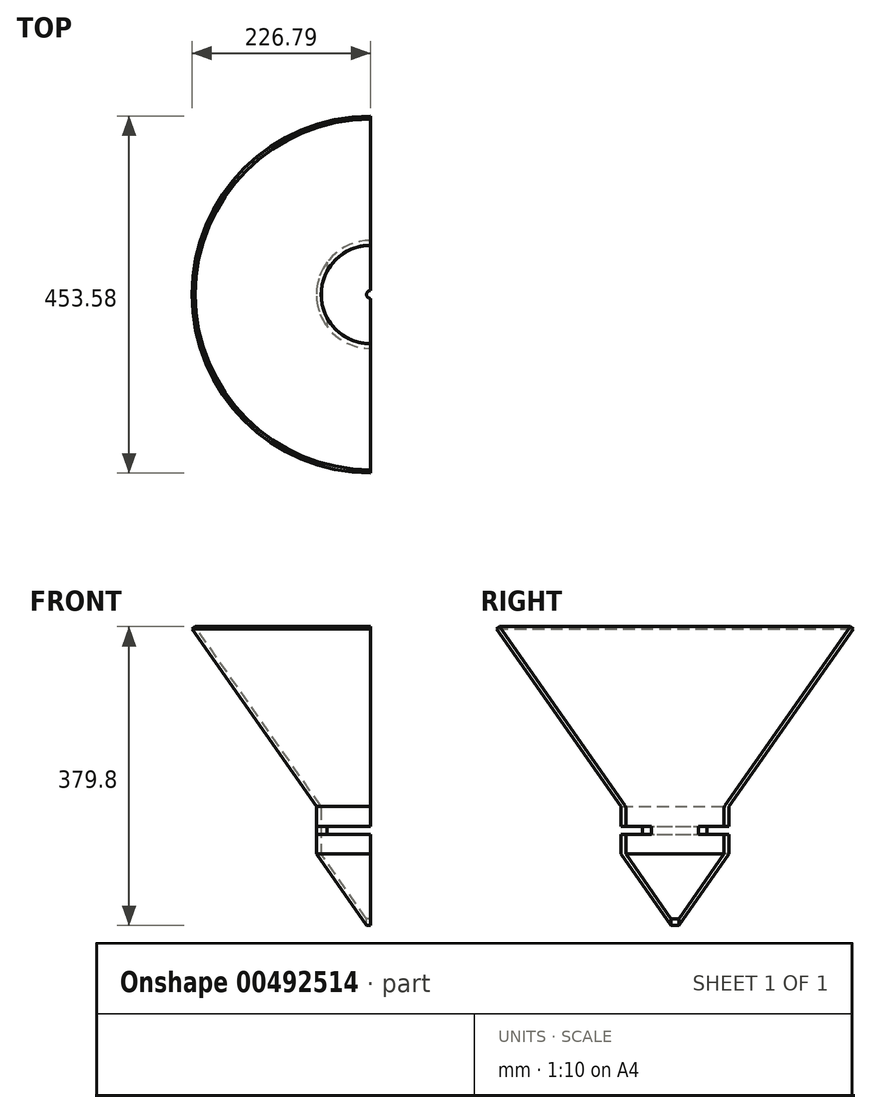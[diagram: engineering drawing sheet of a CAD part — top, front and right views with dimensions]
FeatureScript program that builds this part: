
annotation { "Feature Type Name" : "Feature", "Feature Type Description" : "" }
export const myFeature = defineFeature(function(context is Context, id is Id, definition is map)
    precondition{}
    {
        {
            var Q0;
            Q0=qCreatedBy(makeId("Right.planeOp"),FACE);
            var sketch = newSketch(context, id + "F0", { "sketchPlane" : qUnion([Q0])});
            skLineSegment(sketch, "E0", {"start": v(0, 0) * mm, "end": v(0, 158.91) * mm, "construction": true});
            skLineSegment(sketch, "E1", {"start": v(68.6, 0) * mm, "end": v(226.8, 225.91) * mm});
            skLineSegment(sketch, "E2", {"start": v(63.4, 1.3) * mm, "end": v(222.7, 228.78) * mm});
            skLineSegment(sketch, "E3", {"start": v(62.5, -1.58) * mm, "end": v(62.5, -25.19) * mm});
            skLineSegment(sketch, "E4", {"start": v(68.6, 0) * mm, "end": v(68.6, -25.19) * mm});
            skPoint(sketch, "E5.visualSharp", {"position": v(62.5, 0) * mm});
            skArc(sketch, "E5.filletArc", {"start": v(63.4, 1.3) * mm, "mid": v(62.73, -0.07) * mm, "end": v(62.5, -1.58) * mm});
            skLineSegment(sketch, "E6", {"start": v(62.5, -25.19) * mm, "end": v(68.6, -25.19) * mm});
            skLineSegment(sketch, "E7", {"start": v(222.7, 228.78) * mm, "end": v(222.7, 228.78) * mm});
            skLineSegment(sketch, "E8", {"start": v(222.7, 228.78) * mm, "end": v(226.8, 225.91) * mm});
            skSolve(sketch);
        }
        {
            var Q0;
            Q0 = qSketchRegion(id + "F0", true);
            var Q1;
            Q1=sQuery(id+"F0.wireOp",EDGE,"E0");
            revolve(context, id + "F1", {"entities" : qUnion([Q0]), "axis" : qUnion([Q1]), "revolveType" : RevolveType.ONE_DIRECTION, "angle" : 180 * degree});
        }
        {
            var Q0;
            Q0=makeQuery(id+"F1.opRevolve","SWEPT_FACE",FACE,{"disambiguationData":[OSD([sQuery(id+"F0.wireOp",EDGE,"E6")])]});
            var sketch = newSketch(context, id + "F2", { "sketchPlane" : qUnion([Q0])});
            skArc(sketch, "E9", {"start": v(0, 68.6) * mm, "mid": v(-68.56, 0) * mm, "end": v(0, -68.6) * mm});
            skArc(sketch, "E10", {"start": v(0, 62.5) * mm, "mid": v(-62.5, 0) * mm, "end": v(0, -62.5) * mm});
            skLineSegment(sketch, "E11", {"start": v(-55, -40.95) * mm, "end": v(-55, 41) * mm});
            skSolve(sketch);
        }
        {
            var Q0;
            {var subQ0=sQuery(id+"F2.wireOp",EDGE,"E11");var subQ1=sQuery(id+"F2.wireOp",EDGE,"E9");var subQ2=makeQuery(id+"F2.imprint","INTERSECT",VERTEX,{"disambiguationData":[OD(0.0)],"derivedFrom":[subQ1,subQ0]});Q0=makeQuery(id+"F2.imprint","IMPRINT",FACE,{"disambiguationData":[TD([[makeQuery(id+"F2.imprint","IMPRINT",EDGE,{"disambiguationData":[TD([[subQ2,1.0]])],"derivedFrom":subQ1}),1.0]])]});}
            extrude(context, id + "F3", {"entities" : qUnion([Q0]), "operationType" : NewBodyOperationType.ADD, "depth" : 10 * mm});
        }
        {
            var Q0;
            Q0=makeQuery(id+"F3.opExtrude","CAP_FACE",FACE,{"disambiguationData":[OSD([sQuery(id+"F2.wireOp",EDGE,"E9"),sQuery(id+"F2.wireOp",EDGE,"E10"),sQuery(id+"F2.wireOp",EDGE,"E11")])],"isStart":false});
            var sketch = newSketch(context, id + "F4", { "sketchPlane" : qUnion([Q0])});
            skArc(sketch, "E12.0", {"start": v(-55, -40.95) * mm, "mid": v(-68.56, 0) * mm, "end": v(-55, 40.95) * mm});
            skLineSegment(sketch, "E12.1", {"start": v(-55, -29.69) * mm, "end": v(-55, -40.95) * mm});
            skLineSegment(sketch, "E12.2", {"start": v(-55, 40.95) * mm, "end": v(-55, 29.69) * mm});
            skArc(sketch, "E12.3", {"start": v(0, -62.5) * mm, "mid": v(-32.02, -53.67) * mm, "end": v(-55, -29.69) * mm});
            skArc(sketch, "E12.4", {"start": v(-55, 29.69) * mm, "mid": v(-32.02, 53.67) * mm, "end": v(0, 62.5) * mm});
            skLineSegment(sketch, "E12.5", {"start": v(0, 62.5) * mm, "end": v(0, 68.6) * mm});
            skArc(sketch, "E12.6", {"start": v(0, 68.6) * mm, "mid": v(-68.6, 0) * mm, "end": v(0, -68.6) * mm});
            skLineSegment(sketch, "E12.7", {"start": v(0, -68.6) * mm, "end": v(0, -62.5) * mm});
            skArc(sketch, "E13.0", {"start": v(-55, 40.95) * mm, "mid": v(-68.56, 0) * mm, "end": v(-55, -40.95) * mm});
            skLineSegment(sketch, "E13.1", {"start": v(-55, 29.69) * mm, "end": v(-55, 40.95) * mm});
            skArc(sketch, "E13.2", {"start": v(-55, -29.69) * mm, "mid": v(-62.5, 0) * mm, "end": v(-55, 29.69) * mm});
            skLineSegment(sketch, "E13.3", {"start": v(-55, -40.95) * mm, "end": v(-55, -29.69) * mm});
            skSolve(sketch);
        }
        {
            var Q0;
            Q0 = qSketchRegion(id + "F4", true);
            extrude(context, id + "F5", {"entities" : qUnion([Q0]), "operationType" : NewBodyOperationType.ADD, "depth" : 25 * mm});
        }
        {
            var Q0;
            Q0=qCreatedBy(makeId("Front.planeOp"),FACE);
            var sketch = newSketch(context, id + "F6", { "sketchPlane" : qUnion([Q0])});
            skLineSegment(sketch, "E14", {"start": v(0, 0) * mm, "end": v(0, -90.56) * mm, "construction": true});
            skLineSegment(sketch, "E15.0", {"start": v(0, -60.19) * mm, "end": v(-68.6, -60.19) * mm});
            skLineSegment(sketch, "E16", {"start": v(-68.6, -60.19) * mm, "end": v(-5, -151.02) * mm});
            skLineSegment(sketch, "E17", {"start": v(-62.5, -60.19) * mm, "end": v(-5, -142.3) * mm});
            skLineSegment(sketch, "E18", {"start": v(-5, -142.3) * mm, "end": v(-5, -151.02) * mm});
            skSolve(sketch);
        }
        {
            var Q0;
            Q0 = qSketchRegion(id + "F6", true);
            var Q1;
            Q1=sQuery(id+"F6.wireOp",EDGE,"E14");
            revolve(context, id + "F7", {"operationType" : NewBodyOperationType.ADD, "entities" : qUnion([Q0]), "axis" : qUnion([Q1]), "revolveType" : RevolveType.SYMMETRIC, "angle" : 180 * degree});
        }
    });
